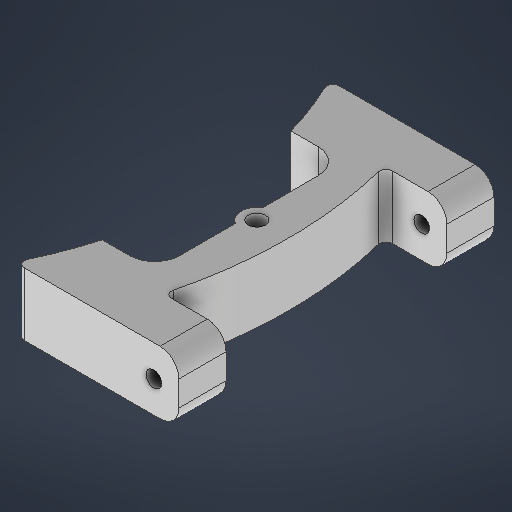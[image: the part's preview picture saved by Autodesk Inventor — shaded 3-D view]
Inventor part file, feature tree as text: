
AUTODESK INVENTOR PART (.ipt)
format: ipt  version: 2025 (Build 290162000, 162)  size: 310,272 bytes
history: native  units: in
note: dims shown in document units (in); Inventor stores cm internally (conversion verified against a paired STEP export)
features: extrude x6, sketch x5, fillet x5, mirror x2, hole x1, projected_geometry x1
ambient origin geometry x8: Origin, YZ Plane, XZ Plane, XY Plane, X Axis, Y Axis, Z Axis, Center Point
bodies: Solid1 (feature_tree)
feature tree (20):
  sketch  "Sketch1"  dims[d0=10.6299in d1=8.6614in]
  extrude  "Extrusion1"  Depth=8.6614in
  extrude  "Extrusion3"  Depth=3.9469in
  fillet  "Fillet1"  Radius=0.9843in
  fillet  "Fillet2"  Radius=0.5906in
  fillet  "Fillet3"  Radius=0.7874in
  hole  "Hole2"  [1 undecoded]
  mirror  "Mirror1"
  mirror  "Mirror2"
  extrude  "Extrusion7"  Depth=0.3937in
  fillet  "Fillet7"  Radius=0.0787in
  extrude  "Extrusion9"  Depth=0.315in
  fillet  "Fillet8"  Radius=0.3937in
  extrude  "Extrusion10"  Depth=0.3937in
  extrude  "Extrusion11"  TaperAngle=0.0deg  [1 undecoded]
  sketch  "Sketch4"  dims[d2=0.7874in d3=0.0in d21=3.9469in d22=0.9843in d23=0.5906in d24=0.7874in]
  projected_geometry  "Projected Loop1"
  sketch  "Sketch5"  dims[d25=0.5906in d26=0.0in d27=0.0in]
  sketch  "Sketch10"  dims[d28=0.2362in d29=0.3937in d30=0.0787in]
  sketch  "Sketch12"  dims[d31=0.1969in d32=0.2362in d33=0.3346in d34=0.1969in d35=90.0deg d36=0.315in d37=0.8108in d38=0.315in d39=0.3937in d57=0.3937in d61=0.0in d62=0.0in d63=0.0787in d68=0.9843in d69=2.3622in d70=0.3937in d71=0.0in d72=0.315in d82=4.9213in d83=180.0deg d84=0.2165in d85=0.3937in d86=0.7874in d87=0.0in d88=0.0in d89=0.0in d81=0.0394in d90=0.0025in d91=0.0295in d92=0.0148in]
note: 2 required parameter values undecoded (feature->parameter linkage not recoverable at this tier; creation-order binding heuristic only, values carry confidence <= 0.55)
